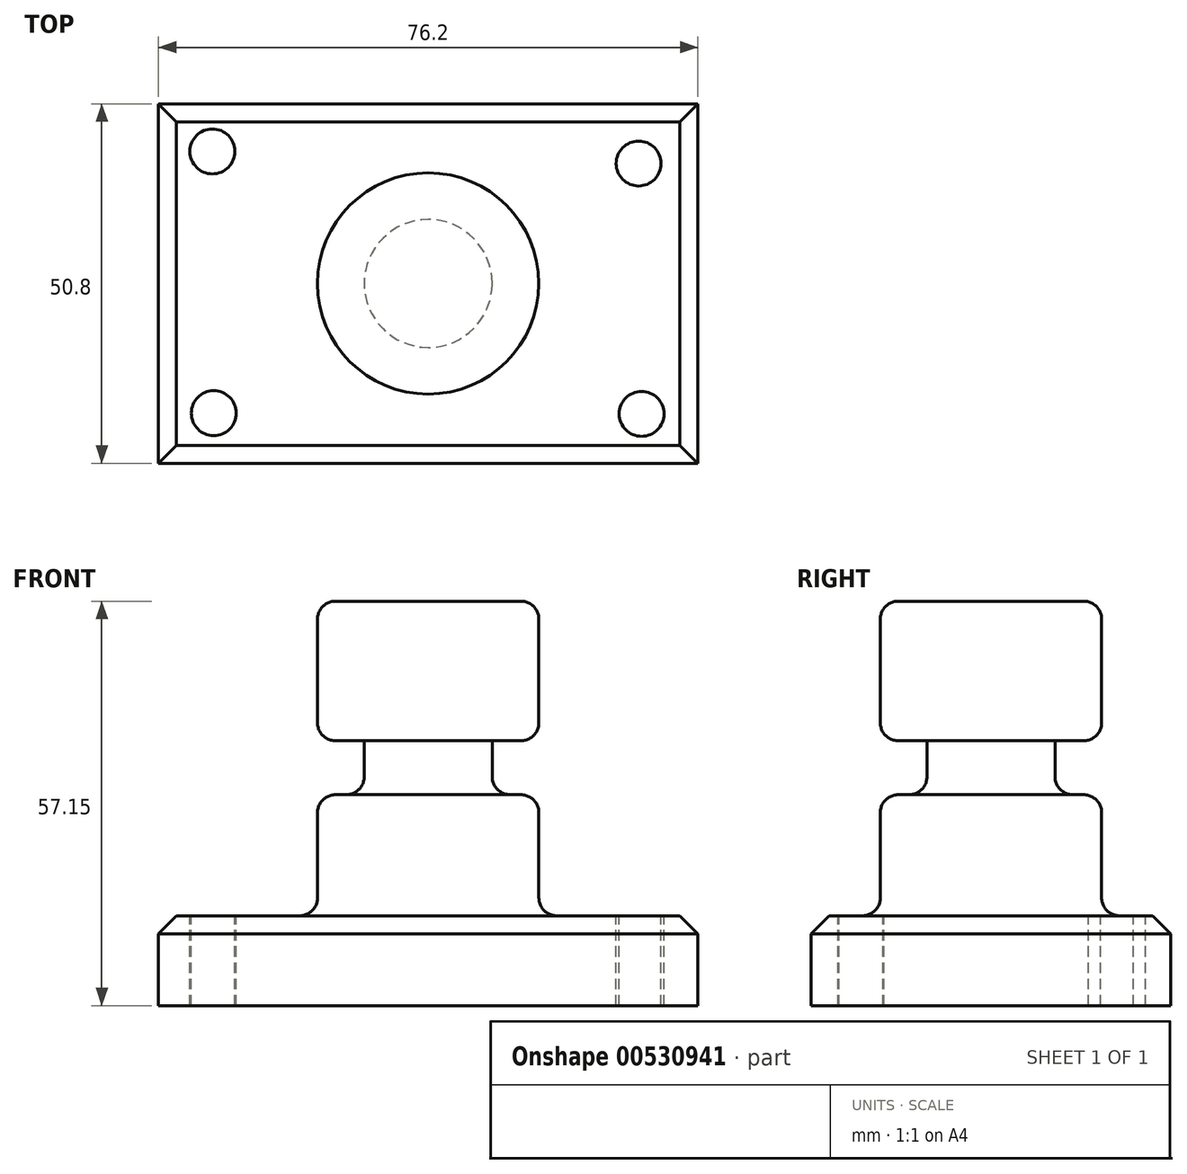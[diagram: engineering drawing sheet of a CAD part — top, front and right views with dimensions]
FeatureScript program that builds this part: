
annotation { "Feature Type Name" : "Feature", "Feature Type Description" : "" }
export const myFeature = defineFeature(function(context is Context, id is Id, definition is map)
    precondition{}
    {
        {
            var Q0;
            Q0=qCreatedBy(makeId("Top.planeOp"),FACE);
            var sketch = newSketch(context, id + "F0", { "sketchPlane" : qUnion([Q0])});
            skLineSegment(sketch, "E0.bottom", {"start": v(-27.94, 25.4) * mm, "end": v(27.94, 25.4) * mm});
            skLineSegment(sketch, "E0.top", {"start": v(-27.94, -25.4) * mm, "end": v(27.94, -25.4) * mm});
            skLineSegment(sketch, "E0.left", {"start": v(-38.1, 15.24) * mm, "end": v(-38.1, -15.24) * mm});
            skLineSegment(sketch, "E0.right", {"start": v(38.1, 15.24) * mm, "end": v(38.1, -15.24) * mm});
            skPoint(sketch, "E0.middle", {"position": v(0, 0) * mm});
            skPoint(sketch, "E1.visualSharp", {"position": v(-38.1, 25.4) * mm});
            skPoint(sketch, "E2.visualSharp", {"position": v(38.1, 25.4) * mm});
            skPoint(sketch, "E3.visualSharp", {"position": v(38.1, -25.4) * mm});
            skPoint(sketch, "E4.visualSharp", {"position": v(-38.1, -25.4) * mm});
            skLineSegment(sketch, "E5", {"start": v(-38.1, 25.4) * mm, "end": v(-38.1, 15.24) * mm});
            skLineSegment(sketch, "E6", {"start": v(-38.1, 25.4) * mm, "end": v(-27.94, 25.4) * mm});
            skLineSegment(sketch, "E7", {"start": v(-38.1, -15.24) * mm, "end": v(-38.1, -25.4) * mm});
            skLineSegment(sketch, "E8", {"start": v(-27.94, -25.4) * mm, "end": v(-38.1, -25.4) * mm});
            skLineSegment(sketch, "E9", {"start": v(27.94, -25.4) * mm, "end": v(38.1, -25.4) * mm});
            skLineSegment(sketch, "E10", {"start": v(38.1, -25.4) * mm, "end": v(38.1, -15.24) * mm});
            skLineSegment(sketch, "E11", {"start": v(38.1, 15.24) * mm, "end": v(38.1, 25.4) * mm});
            skLineSegment(sketch, "E12", {"start": v(38.1, 25.4) * mm, "end": v(27.94, 25.4) * mm});
            skSolve(sketch);
        }
        {
            var Q0;
            {var subQ4=sQuery(id+"F0.wireOp",EDGE,"E5");Q0=makeQuery(id+"F0.imprint","IMPRINT",FACE,{"disambiguationData":[TD([[makeQuery(id+"F0.imprint","IMPRINT",EDGE,{"derivedFrom":subQ4}),1.0]])]});}
            var Q1;
            Q1=makeQuery(id+"F0.imprint","IMPRINT",FACE,{"disambiguationData":[TD([[makeQuery(id+"F0.imprint","IMPRINT",EDGE,{"derivedFrom":sQuery(id+"F0.wireOp",EDGE,"E4.filletArc")}),-1.0]])]});
            var Q2;
            Q2=makeQuery(id+"F0.imprint","IMPRINT",FACE,{"disambiguationData":[TD([[makeQuery(id+"F0.imprint","IMPRINT",EDGE,{"derivedFrom":sQuery(id+"F0.wireOp",EDGE,"E3.filletArc")}),-1.0]])]});
            var Q3;
            Q3=makeQuery(id+"F0.imprint","IMPRINT",FACE,{"disambiguationData":[TD([[makeQuery(id+"F0.imprint","IMPRINT",EDGE,{"derivedFrom":sQuery(id+"F0.wireOp",EDGE,"E2.filletArc")}),-1.0]])]});
            var Q4;
            {var subQ0=sQuery(id+"F0.wireOp",EDGE,"y9Bau404-qRSk-r0Yi-WIpE-xDeAPtF5mR1a");Q4=makeQuery(id+"F0.imprint","IMPRINT",FACE,{"disambiguationData":[TD([[makeQuery(id+"F0.imprint","IMPRINT",EDGE,{"derivedFrom":subQ0}),-1.0]])]});}
            var Q5;
            {var subQ0=sQuery(id+"F0.wireOp",EDGE,"E0.bottom");Q5=makeQuery(id+"F0.imprint","IMPRINT",FACE,{"disambiguationData":[TD([[makeQuery(id+"F0.imprint","IMPRINT",EDGE,{"derivedFrom":subQ0}),-1.0]])]});}
            extrude(context, id + "F1", {"entities" : qUnion([Q0, Q1, Q2, Q3, Q4, Q5]), "depth" : 12.7 * mm, "offsetDistance" : 25.4 * mm});
        }
        {
            var Q0;
            Q0=makeQuery(id+"F1.opExtrude","CAP_FACE",FACE,{"disambiguationData":[OSD([sQuery(id+"F0.wireOp",EDGE,"E0.bottom"),sQuery(id+"F0.wireOp",EDGE,"E0.top"),sQuery(id+"F0.wireOp",EDGE,"E0.left"),sQuery(id+"F0.wireOp",EDGE,"E0.right"),sQuery(id+"F0.wireOp",EDGE,"E5"),sQuery(id+"F0.wireOp",EDGE,"E6"),sQuery(id+"F0.wireOp",EDGE,"E7"),sQuery(id+"F0.wireOp",EDGE,"E8"),sQuery(id+"F0.wireOp",EDGE,"E9"),sQuery(id+"F0.wireOp",EDGE,"E10"),sQuery(id+"F0.wireOp",EDGE,"E11"),sQuery(id+"F0.wireOp",EDGE,"E12")])],"isStart":false});
            var sketch = newSketch(context, id + "F2", { "sketchPlane" : qUnion([Q0])});
            skCircle(sketch, "E13", {"center": v(-30.48, 18.67) * mm, "radius": 3.18 * mm});
            skCircle(sketch, "E14", {"center": v(29.73, 16.95) * mm, "radius": 3.18 * mm});
            skCircle(sketch, "E15", {"center": v(30.15, -18.42) * mm, "radius": 3.18 * mm});
            skCircle(sketch, "E16", {"center": v(-30.29, -18.33) * mm, "radius": 3.18 * mm});
            skSolve(sketch);
        }
        {
            var Q0;
            Q0 = qSketchRegion(id + "F2", true);
            extrude(context, id + "F3", {"entities" : qUnion([Q0]), "operationType" : NewBodyOperationType.REMOVE, "oppositeDirection" : true, "depth" : 25.4 * mm, "offsetDistance" : 25.4 * mm});
        }
        {
            var Q0;
            Q0=qCreatedBy(makeId("Front.planeOp"),FACE);
            var sketch = newSketch(context, id + "F4", { "sketchPlane" : qUnion([Q0])});
            skLineSegment(sketch, "E17.bottom", {"start": v(0, 57.15) * mm, "end": v(15.63, 57.15) * mm});
            skLineSegment(sketch, "E17.top", {"start": v(0, 12.7) * mm, "end": v(15.63, 12.7) * mm});
            skLineSegment(sketch, "E17.left", {"start": v(0, 57.15) * mm, "end": v(0, 12.7) * mm});
            skLineSegment(sketch, "E17.right", {"start": v(15.63, 57.15) * mm, "end": v(15.63, 12.7) * mm});
            skSolve(sketch);
        }
        {
            var Q0;
            Q0=makeQuery(id+"F4.imprint","IMPRINT",FACE,{"disambiguationData":[TD([[makeQuery(id+"F4.imprint","IMPRINT",EDGE,{"derivedFrom":sQuery(id+"F4.wireOp",EDGE,"E17.bottom")}),-1.0]])]});
            var Q1;
            Q1=sQuery(id+"F4.wireOp",EDGE,"E17.left");
            revolve(context, id + "F5", {"operationType" : NewBodyOperationType.ADD, "entities" : qUnion([Q0]), "axis" : qUnion([Q1]), "revolveType" : RevolveType.FULL});
        }
        {
            var Q0;
            Q0=makeQuery(id+"F1.opExtrude","CAP_EDGE",EDGE,{"disambiguationData":[OSD([sQuery(id+"F0.wireOp",EDGE,"E0.top"),sQuery(id+"F0.wireOp",EDGE,"E8"),sQuery(id+"F0.wireOp",EDGE,"E9")])],"isStart":false});
            var Q1;
            Q1=makeQuery(id+"F1.opExtrude","CAP_EDGE",EDGE,{"disambiguationData":[OSD([sQuery(id+"F0.wireOp",EDGE,"E0.right"),sQuery(id+"F0.wireOp",EDGE,"E10"),sQuery(id+"F0.wireOp",EDGE,"E11")])],"isStart":false});
            var Q2;
            Q2=makeQuery(id+"F1.opExtrude","CAP_EDGE",EDGE,{"disambiguationData":[OSD([sQuery(id+"F0.wireOp",EDGE,"E0.bottom"),sQuery(id+"F0.wireOp",EDGE,"E6"),sQuery(id+"F0.wireOp",EDGE,"E12")])],"isStart":false});
            var Q3;
            Q3=makeQuery(id+"F1.opExtrude","CAP_EDGE",EDGE,{"disambiguationData":[OSD([sQuery(id+"F0.wireOp",EDGE,"E0.left"),sQuery(id+"F0.wireOp",EDGE,"E5"),sQuery(id+"F0.wireOp",EDGE,"E7")])],"isStart":false});
            chamfer(context, id + "F6", {"entities" : qUnion([Q0, Q1, Q2, Q3]), "width" : 2.54 * mm, "tangentPropagation" : true});
        }
        {
            var Q0;
            Q0=qCreatedBy(makeId("Front.planeOp"),FACE);
            var sketch = newSketch(context, id + "F7", { "sketchPlane" : qUnion([Q0])});
            skLineSegment(sketch, "E18.bottom", {"start": v(9.04, 37.42) * mm, "end": v(19.2, 37.42) * mm});
            skLineSegment(sketch, "E18.top", {"start": v(11.58, 29.8) * mm, "end": v(19.2, 29.8) * mm});
            skLineSegment(sketch, "E18.left", {"start": v(9.04, 37.42) * mm, "end": v(9.04, 32.34) * mm});
            skLineSegment(sketch, "E18.right", {"start": v(19.2, 37.42) * mm, "end": v(19.2, 29.8) * mm});
            skPoint(sketch, "E19.visualSharp", {"position": v(9.04, 29.8) * mm});
            skArc(sketch, "E19.filletArc", {"start": v(9.04, 32.34) * mm, "mid": v(9.79, 30.55) * mm, "end": v(11.58, 29.8) * mm});
            skSolve(sketch);
        }
        {
            var Q0;
            Q0=makeQuery(id+"F7.imprint","IMPRINT",FACE,{"disambiguationData":[TD([[makeQuery(id+"F7.imprint","IMPRINT",EDGE,{"derivedFrom":sQuery(id+"F7.wireOp",EDGE,"E18.bottom")}),-1.0]])]});
            var Q1;
            Q1=makeQuery(id+"F5.opRevolve","SWEPT_FACE",FACE,{"disambiguationData":[OSD([sQuery(id+"F4.wireOp",EDGE,"E17.right")])]});
            revolve(context, id + "F8", {"operationType" : NewBodyOperationType.REMOVE, "entities" : qUnion([Q0]), "axis" : qUnion([Q1]), "revolveType" : RevolveType.FULL, "oppositeDirection" : true});
        }
        {
            var Q0;
            Q0=makeQuery(id+"F5.opRevolve","SWEPT_EDGE",EDGE,{"disambiguationData":[OSD([sQuery(id+"F4.wireOp",EDGE,"E17.top"),sQuery(id+"F4.wireOp",EDGE,"E17.right")])]});
            var Q1;
            Q1=makeQuery(id+"F5.opRevolve","SWEPT_EDGE",EDGE,{"disambiguationData":[OSD([sQuery(id+"F4.wireOp",EDGE,"E17.bottom"),sQuery(id+"F4.wireOp",EDGE,"E17.right")])]});
            var Q2;
            Q2=makeQuery(id+"F5.opRevolve","SWEPT_FACE",FACE,{"disambiguationData":[OSD([sQuery(id+"F4.wireOp",EDGE,"E17.right")])]});
            fillet(context, id + "F9", {"entities" : qUnion([Q0, Q1, Q2]), "radius" : 2.54 * mm, "tangentPropagation" : true, "allowEdgeOverflow" : false});
        }
    });
